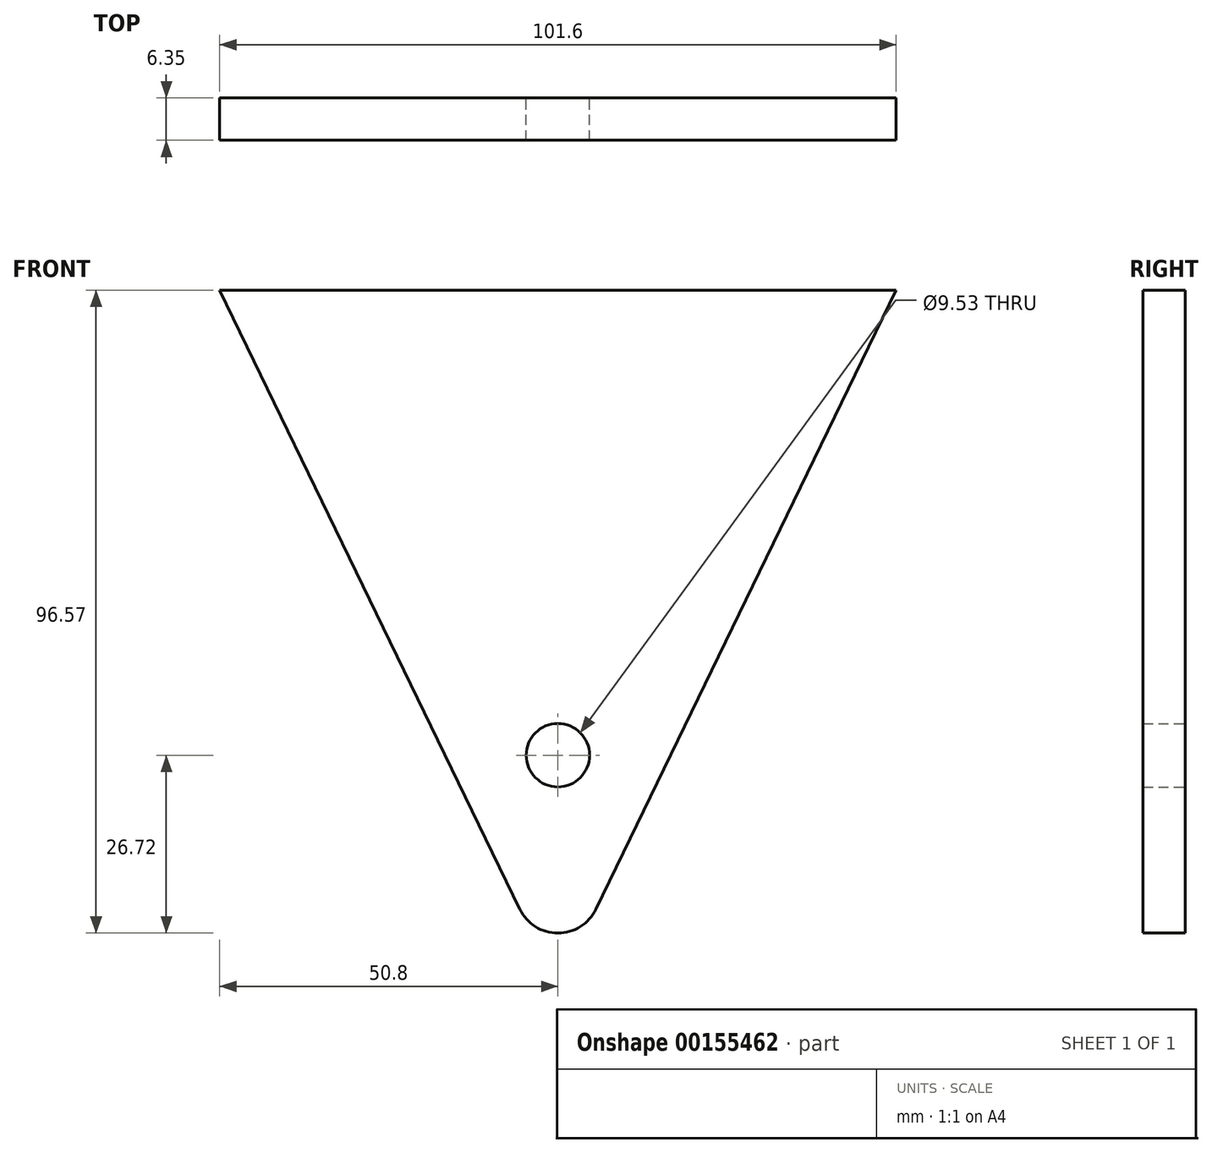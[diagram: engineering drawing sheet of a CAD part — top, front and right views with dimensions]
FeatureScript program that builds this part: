
annotation { "Feature Type Name" : "Feature", "Feature Type Description" : "" }
export const myFeature = defineFeature(function(context is Context, id is Id, definition is map)
    precondition{}
    {
        {
            var Q0;
            Q0=qCreatedBy(makeId("Front.planeOp"),FACE);
            var sketch = newSketch(context, id + "F0", { "sketchPlane" : qUnion([Q0])});
            skCircle(sketch, "E0", {"center": v(0, 0) * mm, "radius": 4.76 * mm});
            skLineSegment(sketch, "E1", {"start": v(-50.8, 69.85) * mm, "end": v(50.8, 69.85) * mm});
            skLineSegment(sketch, "E2", {"start": v(-50.8, 69.85) * mm, "end": v(-5.71, -23.14) * mm});
            skLineSegment(sketch, "E3", {"start": v(5.71, -23.14) * mm, "end": v(50.8, 69.85) * mm});
            skPoint(sketch, "E4.visualSharp", {"position": v(0, -34.93) * mm});
            skArc(sketch, "E4.filletArc", {"start": v(-5.71, -23.14) * mm, "mid": v(0, -26.72) * mm, "end": v(5.71, -23.14) * mm});
            skSolve(sketch);
        }
        {
            var Q0;
            Q0 = qSketchRegion(id + "F0", true);
            extrude(context, id + "F1", {"entities" : qUnion([Q0]), "depth" : 6.35 * mm});
        }
    });
